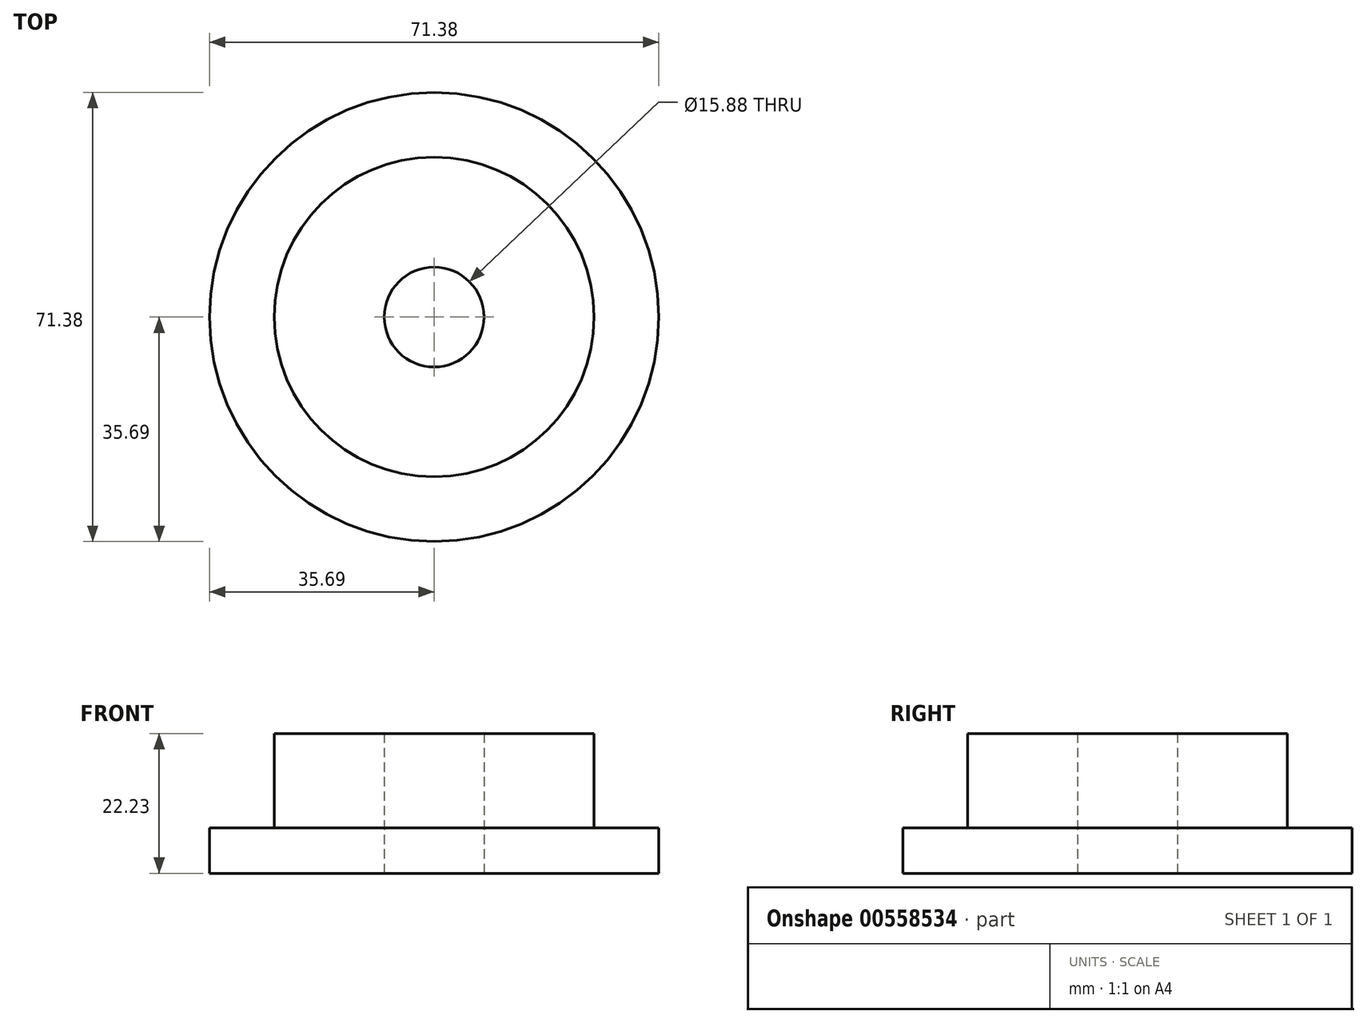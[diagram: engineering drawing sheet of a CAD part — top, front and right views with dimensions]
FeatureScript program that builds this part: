
annotation { "Feature Type Name" : "Feature", "Feature Type Description" : "" }
export const myFeature = defineFeature(function(context is Context, id is Id, definition is map)
    precondition{}
    {
        {
            assignVariable(context, id + "F0", {"name" : "sprocket", "anyValue" : 22.22 * mm});
        }
        {
            assignVariable(context, id + "F1", {"name" : "gear_thickness", "anyValue" : 7.2 * mm});
        }
        {
            var Q0;
            Q0=qCreatedBy(makeId("Top.planeOp"),FACE);
            var sketch = newSketch(context, id + "F2", { "sketchPlane" : qUnion([Q0])});
            skCircle(sketch, "E0", {"center": v(0, 0) * mm, "radius": 35.69 * mm});
            skCircle(sketch, "E1", {"center": v(0, 0) * mm, "radius": 25.4 * mm});
            skCircle(sketch, "E2", {"center": v(0, 0) * mm, "radius": 7.94 * mm});
            skSolve(sketch);
        }
        {
            var Q0;
            Q0=makeQuery(id+"F2.imprint","IMPRINT",FACE,{"disambiguationData":[TD([[makeQuery(id+"F2.imprint","IMPRINT",EDGE,{"derivedFrom":sQuery(id+"F2.wireOp",EDGE,"E1")}),1.0]])]});
            extrude(context, id + "F3", {"entities" : qUnion([Q0]), "depth" : getVariable(context, 'sprocket'), "offsetDistance" : 25 * mm});
        }
        {
            var Q0;
            Q0=makeQuery(id+"F2.imprint","IMPRINT",FACE,{"disambiguationData":[TD([[makeQuery(id+"F2.imprint","IMPRINT",EDGE,{"derivedFrom":sQuery(id+"F2.wireOp",EDGE,"E0")}),1.0]])]});
            extrude(context, id + "F4", {"entities" : qUnion([Q0]), "operationType" : NewBodyOperationType.ADD, "depth" : getVariable(context, 'gear_thickness'), "offsetDistance" : 25 * mm});
        }
    });
